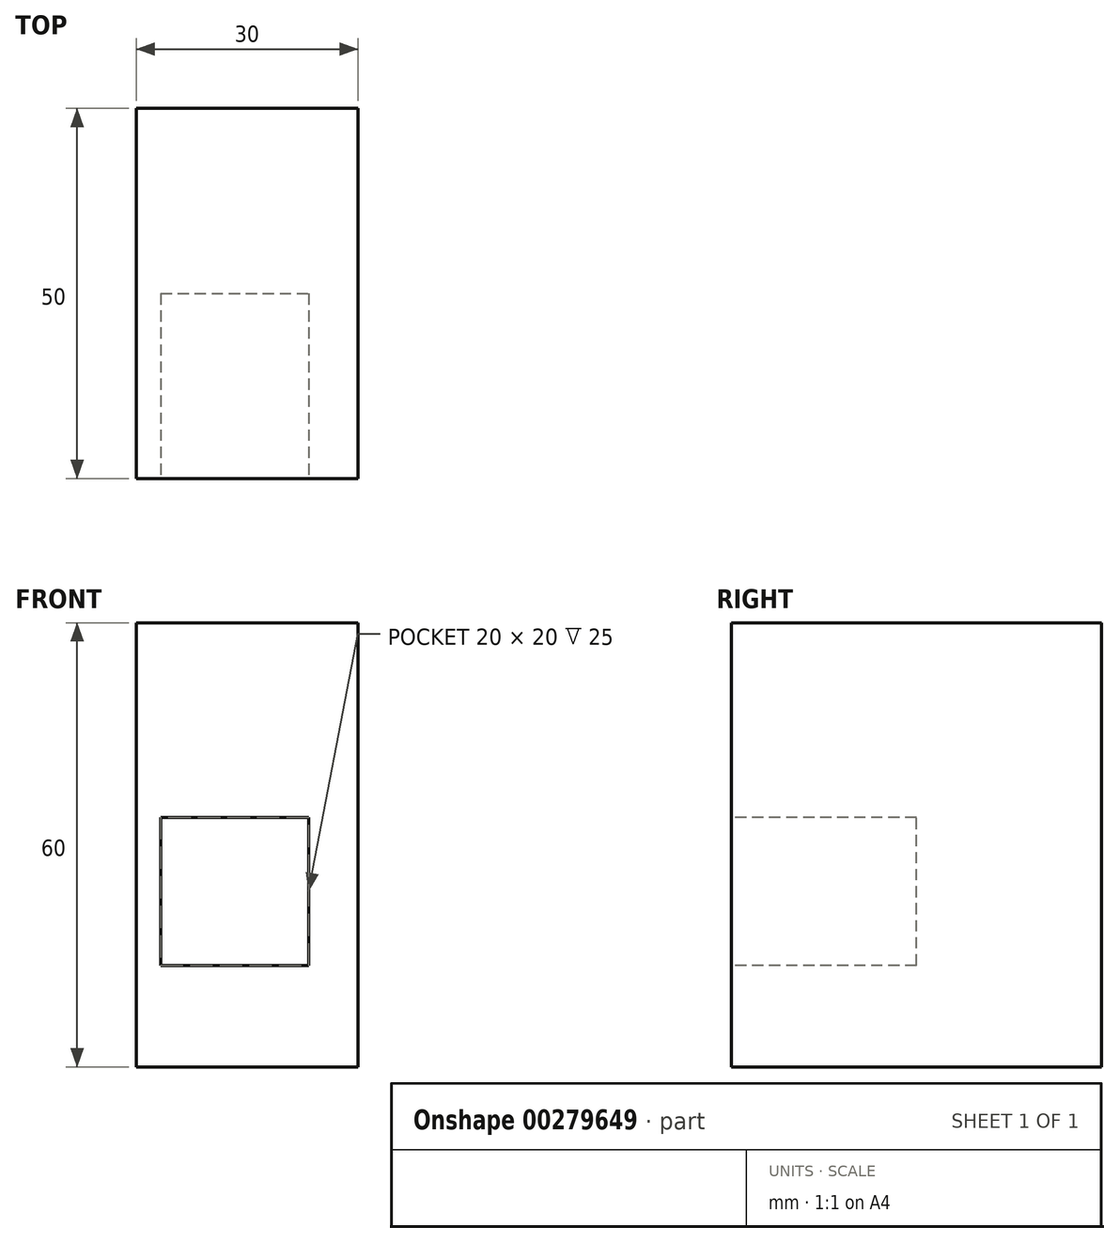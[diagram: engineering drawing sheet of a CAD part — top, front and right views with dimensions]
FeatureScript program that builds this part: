
annotation { "Feature Type Name" : "Feature", "Feature Type Description" : "" }
export const myFeature = defineFeature(function(context is Context, id is Id, definition is map)
    precondition{}
    {
        {
            var Q0;
            Q0=qCreatedBy(makeId("Front.planeOp"),FACE);
            var sketch = newSketch(context, id + "F0", { "sketchPlane" : qUnion([Q0])});
            skLineSegment(sketch, "E0.bottom", {"start": v(0, 0) * mm, "end": v(-30, 0) * mm});
            skLineSegment(sketch, "E0.top", {"start": v(0, 60) * mm, "end": v(-30, 60) * mm});
            skLineSegment(sketch, "E0.left", {"start": v(0, 0) * mm, "end": v(0, 60) * mm});
            skLineSegment(sketch, "E0.right", {"start": v(-30, 0) * mm, "end": v(-30, 60) * mm});
            skSolve(sketch);
        }
        {
            var Q0;
            Q0=makeQuery(id+"F0.imprint","IMPRINT",FACE,{"disambiguationData":[TD([[makeQuery(id+"F0.imprint","IMPRINT",EDGE,{"derivedFrom":sQuery(id+"F0.wireOp",EDGE,"E0.bottom")}),-1.0]])]});
            extrude(context, id + "F1", {"entities" : qUnion([Q0]), "depth" : 50 * mm});
        }
        {
            var Q0;
            Q0=makeQuery(id+"F1.opExtrude","CAP_FACE",FACE,{"disambiguationData":[OSD([sQuery(id+"F0.wireOp",EDGE,"E0.bottom"),sQuery(id+"F0.wireOp",EDGE,"E0.top"),sQuery(id+"F0.wireOp",EDGE,"E0.left"),sQuery(id+"F0.wireOp",EDGE,"E0.right")])],"isStart":false});
            var sketch = newSketch(context, id + "F2", { "sketchPlane" : qUnion([Q0])});
            skLineSegment(sketch, "E1.bottom", {"start": v(-26.68, 13.72) * mm, "end": v(-6.68, 13.72) * mm});
            skLineSegment(sketch, "E1.top", {"start": v(-26.68, 33.72) * mm, "end": v(-6.68, 33.72) * mm});
            skLineSegment(sketch, "E1.left", {"start": v(-26.68, 13.72) * mm, "end": v(-26.68, 33.72) * mm});
            skLineSegment(sketch, "E1.right", {"start": v(-6.68, 13.72) * mm, "end": v(-6.68, 33.72) * mm});
            skSolve(sketch);
        }
        {
            var Q0;
            Q0=makeQuery(id+"F2.imprint","IMPRINT",FACE,{"disambiguationData":[TD([[makeQuery(id+"F2.imprint","IMPRINT",EDGE,{"derivedFrom":sQuery(id+"F2.wireOp",EDGE,"E1.bottom")}),1.0]])]});
            var sketch = newSketch(context, id + "F3", { "sketchPlane" : qUnion([Q0])});
            skSolve(sketch);
        }
        {
            var Q0;
            Q0=makeQuery(id+"F3.imprint","IMPRINT",FACE,{"disambiguationData":[TD([[makeQuery(id+"F3.imprint","IMPRINT",EDGE,{"derivedFrom":makeQuery(id+"F2.imprint","IMPRINT",EDGE,{"derivedFrom":sQuery(id+"F2.wireOp",EDGE,"E1.bottom")})}),1.0]])]});
            extrude(context, id + "F4", {"entities" : qUnion([Q0]), "operationType" : NewBodyOperationType.REMOVE, "oppositeDirection" : true, "depth" : 25 * mm});
        }
    });
